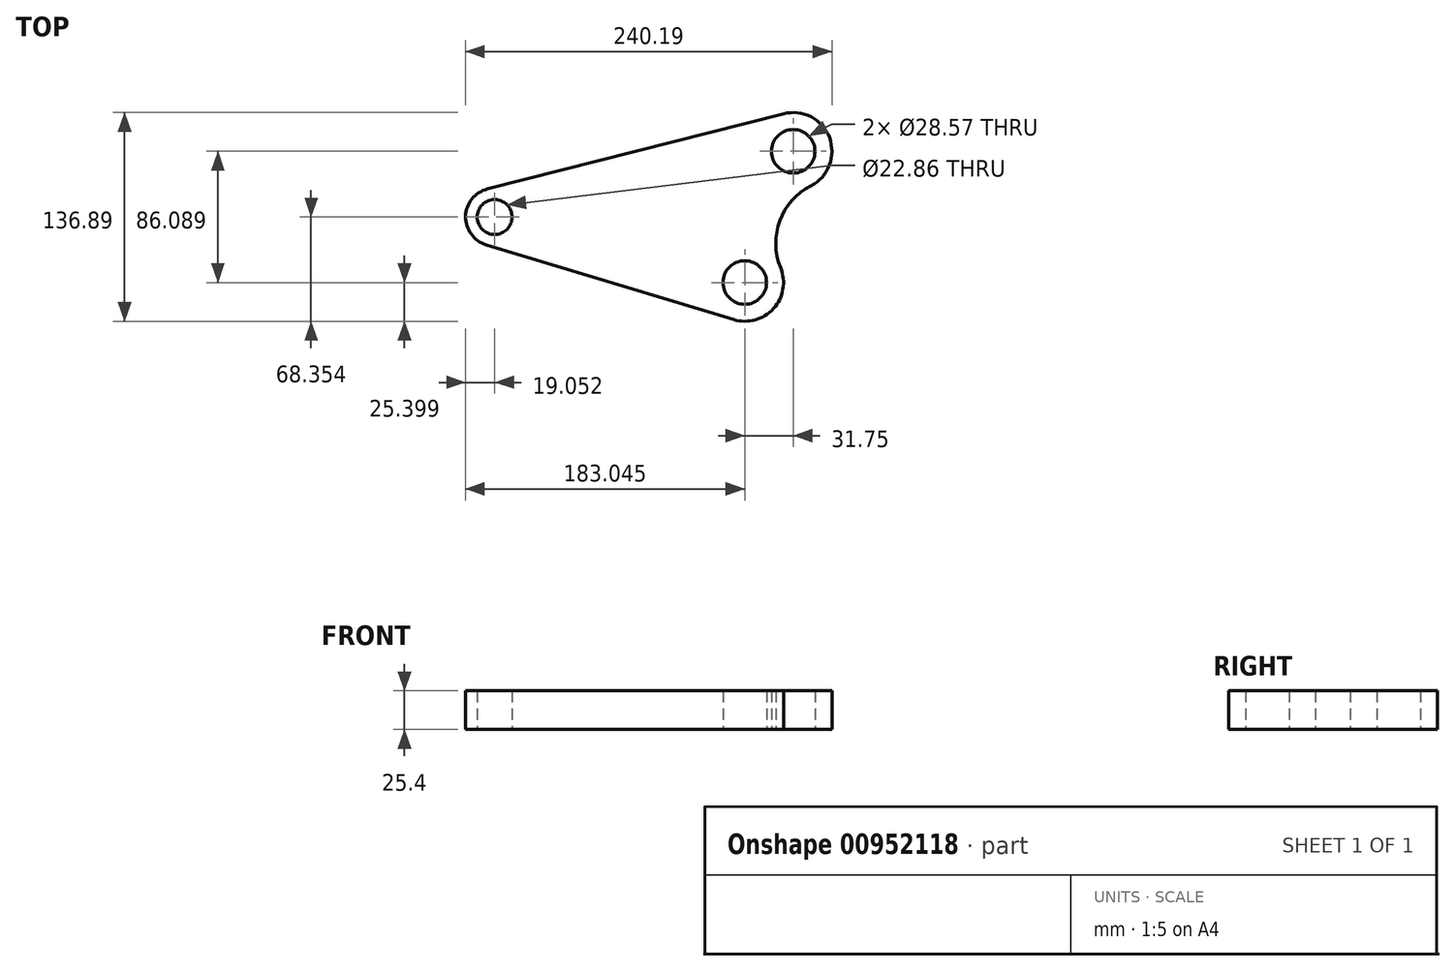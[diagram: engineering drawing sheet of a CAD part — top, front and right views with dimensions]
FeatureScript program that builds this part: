
annotation { "Feature Type Name" : "Feature", "Feature Type Description" : "" }
export const myFeature = defineFeature(function(context is Context, id is Id, definition is map)
    precondition{}
    {
        {
            var Q0;
            Q0=qCreatedBy(makeId("Top.planeOp"),FACE);
            var sketch = newSketch(context, id + "F0", { "sketchPlane" : qUnion([Q0])});
            skCircle(sketch, "E0", {"center": v(-219.08, 50.66) * mm, "radius": 11.43 * mm});
            skCircle(sketch, "E1", {"center": v(-23.34, 93.8) * mm, "radius": 14.29 * mm});
            skCircle(sketch, "E2", {"center": v(-55.09, 7.7) * mm, "radius": 14.29 * mm});
            skCircle(sketch, "E3", {"center": v(-55.09, 7.7) * mm, "radius": 21.59 * mm, "construction": true});
            skCircle(sketch, "E4", {"center": v(-23.34, 93.8) * mm, "radius": 20.64 * mm, "construction": true});
            skLineSegment(sketch, "E5", {"start": v(-23.34, 93.8) * mm, "end": v(-55.09, 93.8) * mm, "construction": true});
            skLineSegment(sketch, "E6", {"start": v(-55.09, 93.8) * mm, "end": v(-55.09, 7.7) * mm, "construction": true});
            skCircle(sketch, "E7", {"center": v(-219.08, 50.66) * mm, "radius": 19.05 * mm});
            skCircle(sketch, "E8", {"center": v(-55.09, 7.7) * mm, "radius": 25.4 * mm});
            skCircle(sketch, "E9", {"center": v(-23.34, 93.8) * mm, "radius": 25.4 * mm});
            skLineSegment(sketch, "E10", {"start": v(-223.77, 69.13) * mm, "end": v(-29.58, 118.42) * mm});
            skArc(sketch, "E11", {"start": v(-11.71, 71.21) * mm, "mid": v(-32.13, 48.14) * mm, "end": v(-31.58, 17.34) * mm});
            skLineSegment(sketch, "E12", {"start": v(-224.6, 32.43) * mm, "end": v(-62.44, -16.6) * mm});
            skSolve(sketch);
        }
        {
            var Q0;
            {var subQ0=sQuery(id+"F0.wireOp",EDGE,"E10");Q0=makeQuery(id+"F0.imprint","IMPRINT",FACE,{"disambiguationData":[TD([[makeQuery(id+"F0.imprint","IMPRINT",EDGE,{"derivedFrom":subQ0}),-1.0]])]});}
            var Q1;
            Q1=makeQuery(id+"F0.imprint","IMPRINT",FACE,{"disambiguationData":[TD([[makeQuery(id+"F0.imprint","IMPRINT",EDGE,{"derivedFrom":sQuery(id+"F0.wireOp",EDGE,"E0")}),-1.0]])]});
            var Q2;
            Q2=makeQuery(id+"F0.imprint","IMPRINT",FACE,{"disambiguationData":[TD([[makeQuery(id+"F0.imprint","IMPRINT",EDGE,{"derivedFrom":sQuery(id+"F0.wireOp",EDGE,"E1")}),-1.0]])]});
            var Q3;
            Q3=makeQuery(id+"F0.imprint","IMPRINT",FACE,{"disambiguationData":[TD([[makeQuery(id+"F0.imprint","IMPRINT",EDGE,{"derivedFrom":sQuery(id+"F0.wireOp",EDGE,"E2")}),-1.0]])]});
            extrude(context, id + "F1", {"entities" : qUnion([Q0, Q1, Q2, Q3]), "depth" : 25.4 * mm, "offsetDistance" : 25.4 * mm});
        }
    });
